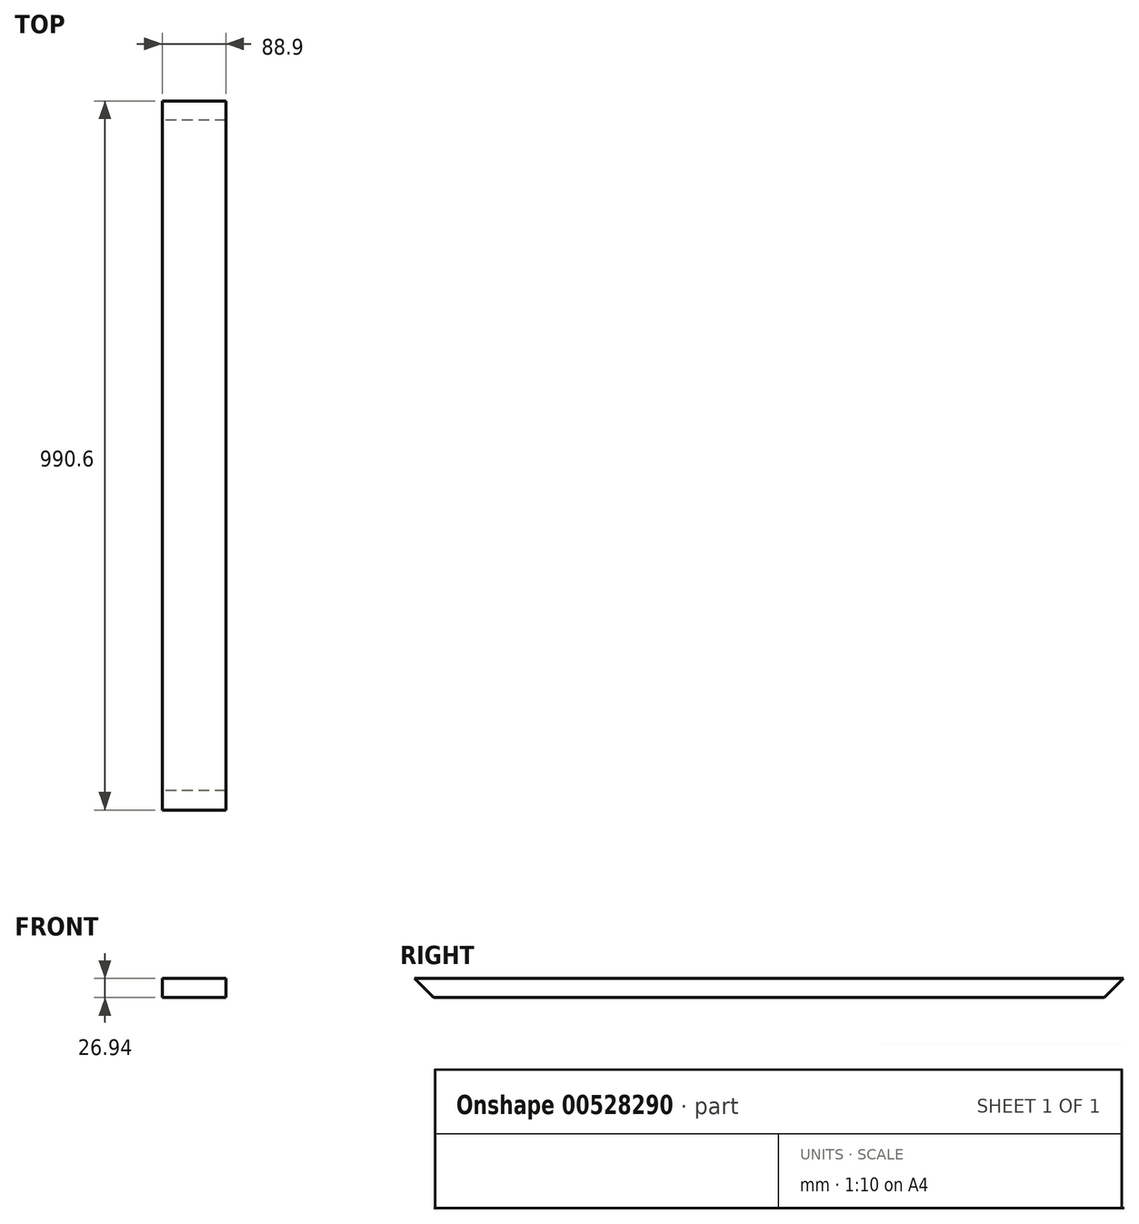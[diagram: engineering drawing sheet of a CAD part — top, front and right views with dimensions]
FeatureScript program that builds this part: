
annotation { "Feature Type Name" : "Feature", "Feature Type Description" : "" }
export const myFeature = defineFeature(function(context is Context, id is Id, definition is map)
    precondition{}
    {
        {
            var Q0;
            Q0=qCreatedBy(makeId("Right.planeOp"),FACE);
            var sketch = newSketch(context, id + "F0", { "sketchPlane" : qUnion([Q0])});
            skLineSegment(sketch, "E0", {"start": v(-506.34, 26.94) * mm, "end": v(484.26, 26.94) * mm});
            skLineSegment(sketch, "E1", {"start": v(-506.34, 26.94) * mm, "end": v(-479.4, 0) * mm});
            skLineSegment(sketch, "E2", {"start": v(484.26, 26.94) * mm, "end": v(457.32, 0) * mm});
            skLineSegment(sketch, "E3", {"start": v(-479.4, 0) * mm, "end": v(457.32, 0) * mm});
            skSolve(sketch);
        }
        {
            var Q0;
            Q0 = qSketchRegion(id + "F0", true);
            extrude(context, id + "F1", {"entities" : qUnion([Q0]), "depth" : 88.9 * mm, "offsetDistance" : 25.4 * mm});
        }
    });
